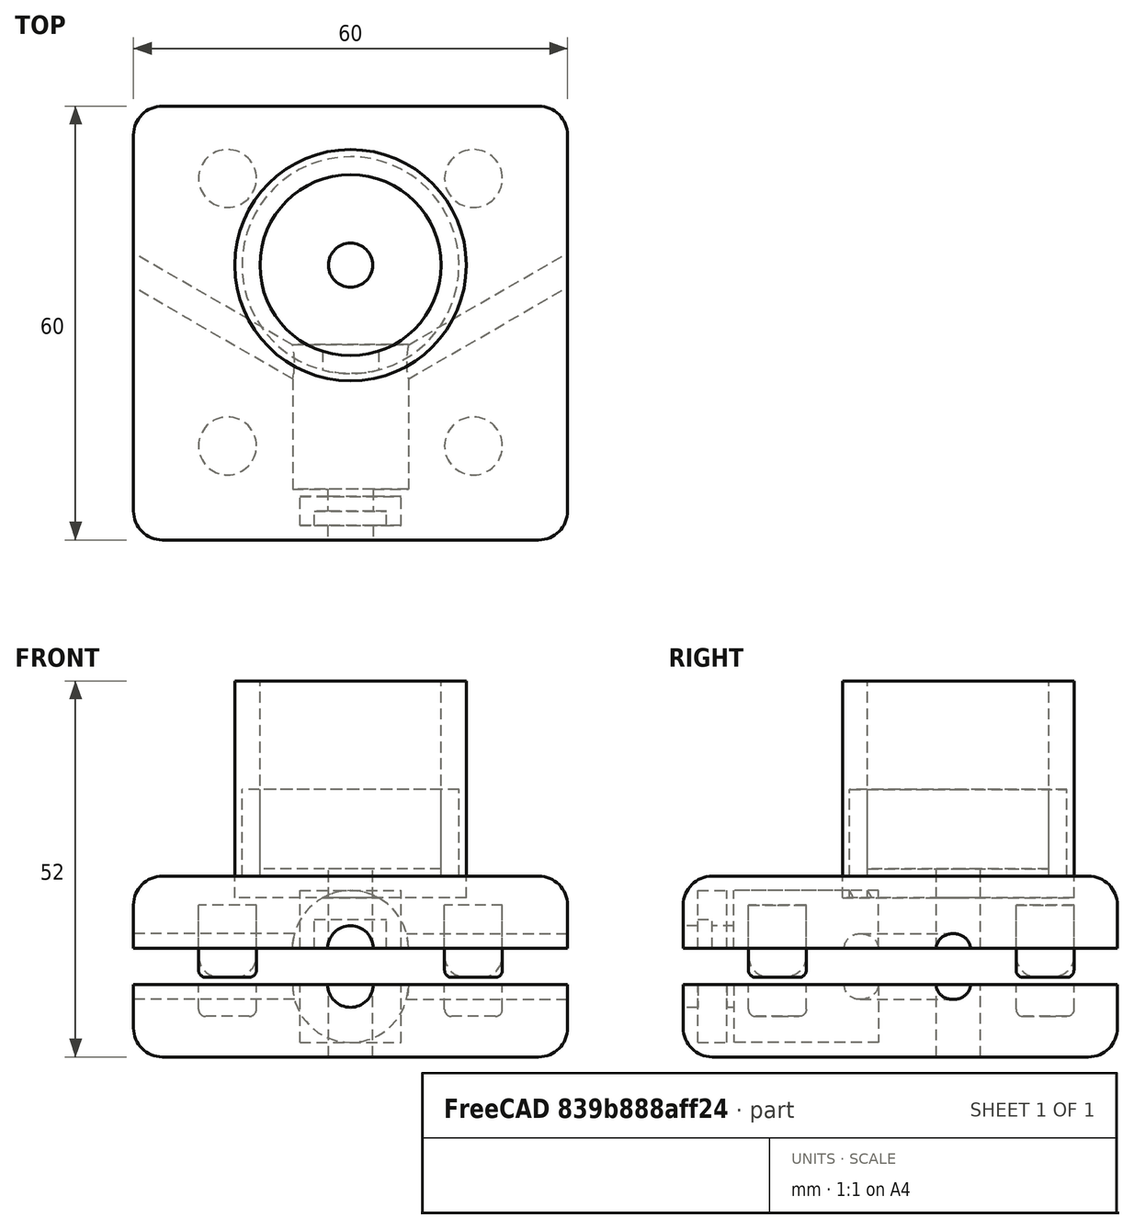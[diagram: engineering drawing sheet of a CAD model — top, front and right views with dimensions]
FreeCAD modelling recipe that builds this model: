
FCSTD DOCUMENT  (FreeCAD 0.18R4 (GitTag))
Label: V-Dipole_VHF_v07
License: All rights reserved
LicenseURL: http://en.wikipedia.org/wiki/All_rights_reserved
objects: Part::Cylinder×32, Part::Fillet×15, Part::MultiFuse×11, Part::Cut×10, Part::Box×6
note: 74 computed .brp shape members not serialized (recipe doc carries the construction recipe); baked Part::Feature solids carry a one-line shape summary decoded from their .brp

FEATURE [Part::Box] Box  label="Cubo"
  AttacherType = Attacher::AttachEngine3D
  Height = 10
  Length = 60
  Width = 60
FEATURE [Part::Fillet] Fillet  label="FilletA"
  Base = -> Box
  Edges = 8 edges r=4: [Edge1,Edge2,Edge3,Edge5,Edge6,Edge7,Edge10,Edge12]
FEATURE [Part::Box] Box001  label="Cubo001"
  AttacherType = Attacher::AttachEngine3D
  Height = 10
  Length = 60
  Width = 60
FEATURE [Part::Fillet] Fillet001  label="FilletB"
  Base = -> Box001
  Edges = 8 edges r=4: [Edge1,Edge2,Edge3,Edge5,Edge6,Edge7,Edge10,Edge12]
  Placement = pos=(0,60,-5) rot=(1,0,0;3.14159rad)
FEATURE [Part::Cylinder] Cylinder017  label="RamoA1"
  Angle = 360
  AttacherType = Attacher::AttachEngine3D
  Height = 100
  Placement = pos=(30,20,0) rot=(-0.774597,-0.447214,0.447214;1.82348rad)
  Radius = 2.05
FEATURE [Part::Cylinder] Cylinder018  label="RamoA2"
  Angle = 360
  AttacherType = Attacher::AttachEngine3D
  Height = 100
  Placement = pos=(30,20,0) rot=(-0.774597,0.447214,-0.447214;1.82348rad)
  Radius = 2.05
FEATURE [Part::Cylinder] Cylinder019  label="RamoB1"
  Angle = 360
  AttacherType = Attacher::AttachEngine3D
  Height = 100
  Placement = pos=(30,20,-5) rot=(-0.774597,-0.447214,0.447214;1.82348rad)
  Radius = 2.05
FEATURE [Part::Cylinder] Cylinder020  label="RamoB2"
  Angle = 360
  AttacherType = Attacher::AttachEngine3D
  Height = 100
  Placement = pos=(30,20,-5) rot=(-0.774597,0.447214,-0.447214;1.82348rad)
  Radius = 2.05
FEATURE [Part::Cylinder] Cylinder003  label="ForoBM3"
  Angle = 360
  AttacherType = Attacher::AttachEngine3D
  Height = 60
  Placement = pos=(30,38,-30) rot=(0,0,1;0rad)
  Radius = 3.05
FEATURE [Part::Cylinder] Cylinder014  label="CilindroInterno"
  Angle = 360
  AttacherType = Attacher::AttachEngine3D
  Height = 17
  Placement = pos=(30,38,6) rot=(0,0,1;0rad)
  Radius = 12.52
FEATURE [Part::Cylinder] Cylinder015  label="CilindroEsterno"
  Angle = 360
  AttacherType = Attacher::AttachEngine3D
  Height = 15
  Placement = pos=(30,38,7) rot=(0,0,1;0rad)
  Radius = 15
FEATURE [Part::Cut] Cut019  label="Supporto"
  Base = -> Cylinder015
  Tool = -> Cylinder014
FEATURE [Part::Cylinder] Cylinder  label="CilindroA"
  Angle = 360
  AttacherType = Attacher::AttachEngine3D
  Height = 26
  Placement = pos=(30,24,0) rot=(1,0,0;1.5708rad)
  Radius = 3.15
FEATURE [Part::Cylinder] Cylinder016  label="CilindroB"
  Angle = 360
  AttacherType = Attacher::AttachEngine3D
  Height = 26
  Placement = pos=(30,24,-5) rot=(1,0,0;1.5708rad)
  Radius = 3.15
FEATURE [Part::Box] Box005  label="CuboA"
  AttacherType = Attacher::AttachEngine3D
  Height = 8
  Length = 10
  Placement = pos=(25,2,-4) rot=(0,0,1;0rad)
  Width = 2
FEATURE [Part::Box] Box006  label="CuboB"
  AttacherType = Attacher::AttachEngine3D
  Height = 12
  Length = 14
  Placement = pos=(23,2,-13) rot=(0,0,1;0rad)
  Width = 4
FEATURE [Part::Cylinder] Cylinder021  label="CilindroA2"
  Angle = 360
  AttacherType = Attacher::AttachEngine3D
  Height = 20
  Placement = pos=(30,27,0) rot=(1,0,0;1.5708rad)
  Radius = 8
FEATURE [Part::MultiFuse] Fusion  label="FusionA"
  Shapes = -> [Cylinder017,Cylinder018,Cylinder,Box005,Cylinder021]
FEATURE [Part::Cylinder] Cylinder022  label="CilindroB2"
  Angle = 360
  AttacherType = Attacher::AttachEngine3D
  Height = 20
  Placement = pos=(30,27,-5) rot=(1,0,0;1.5708rad)
  Radius = 8
FEATURE [Part::MultiFuse] Fusion001
  Shapes = -> [Cylinder019,Cylinder020,Cylinder016,Box006,Cylinder022]
FEATURE [Part::Cut] Cut  label="FusionB"
  Base = -> Fillet001
  Tool = -> Fusion001
FEATURE [Part::Cylinder] Cylinder023  label="ForoAM3"
  Angle = 360
  AttacherType = Attacher::AttachEngine3D
  Height = 60
  Placement = pos=(30,38,-30) rot=(0,0,1;0rad)
  Radius = 3.05
FEATURE [Part::Cut] Cut020  label="ConchigliaB"
  Base = -> Cut
  Tool = -> Cylinder003
FEATURE [Part::Cut] Cut021
  Base = -> Fillet
  Tool = -> Fusion
FEATURE [Part::Cut] Cut022
  Base = -> Cut021
  Tool = -> Cylinder023
FEATURE [Part::MultiFuse] Fusion002  label="ConchigliaA"
  Shapes = -> [Cut019,Cut022]
FEATURE [Part::Cylinder] Cylinder024  label="CilindroA10"
  Angle = 360
  AttacherType = Attacher::AttachEngine3D
  Height = 10
  Placement = pos=(13,13,-4) rot=(0,0,1;0rad)
  Radius = 4
FEATURE [Part::Cylinder] Cylinder025  label="CilindroA11"
  Angle = 360
  AttacherType = Attacher::AttachEngine3D
  Height = 10
  Placement = pos=(47,13,-4) rot=(0,0,1;0rad)
  Radius = 4
FEATURE [Part::Fillet] Fillet002
  Base = -> Cylinder024
  Edges = 1 edges r=3: [Edge3]
FEATURE [Part::Fillet] Fillet003
  Base = -> Cylinder025
  Edges = 1 edges r=3: [Edge3]
FEATURE [Part::Cylinder] Cylinder026  label="CilindroA012"
  Angle = 360
  AttacherType = Attacher::AttachEngine3D
  Height = 10
  Placement = pos=(13,13,-4) rot=(0,0,1;0rad)
  Radius = 4
FEATURE [Part::Cylinder] Cylinder027  label="CilindroA013"
  Angle = 360
  AttacherType = Attacher::AttachEngine3D
  Height = 10
  Placement = pos=(47,13,-4) rot=(0,0,1;0rad)
  Radius = 4
FEATURE [Part::Fillet] Fillet004
  Base = -> Cylinder027
  Edges = 1 edges r=3: [Edge3]
  Placement = pos=(0,37,0) rot=(0,0,1;0rad)
FEATURE [Part::Fillet] Fillet005
  Base = -> Cylinder026
  Edges = 1 edges r=3: [Edge3]
  Placement = pos=(0,37,0) rot=(0,0,1;0rad)
FEATURE [Part::Cylinder] Cylinder028  label="CilindroA014"
  Angle = 360
  AttacherType = Attacher::AttachEngine3D
  Height = 10
  Placement = pos=(13,13,-4) rot=(0,0,1;0rad)
  Radius = 4
FEATURE [Part::Cylinder] Cylinder029  label="CilindroA015"
  Angle = 360
  AttacherType = Attacher::AttachEngine3D
  Height = 10
  Placement = pos=(13,13,-4) rot=(0,0,1;0rad)
  Radius = 4
FEATURE [Part::Cylinder] Cylinder030  label="CilindroA016"
  Angle = 360
  AttacherType = Attacher::AttachEngine3D
  Height = 10
  Placement = pos=(47,13,-4) rot=(0,0,1;0rad)
  Radius = 4
FEATURE [Part::Cylinder] Cylinder031  label="CilindroA017"
  Angle = 360
  AttacherType = Attacher::AttachEngine3D
  Height = 10
  Placement = pos=(47,13,-4) rot=(0,0,1;0rad)
  Radius = 4
FEATURE [Part::Fillet] Fillet006
  Base = -> Cylinder029
  Edges = 1 edges r=1: [Edge3]
  Placement = pos=(0,37,0) rot=(0,0,1;0rad)
FEATURE [Part::Fillet] Fillet007
  Base = -> Cylinder030
  Edges = 1 edges r=1: [Edge3]
FEATURE [Part::Fillet] Fillet008
  Base = -> Cylinder028
  Edges = 1 edges r=1: [Edge3]
FEATURE [Part::Fillet] Fillet009
  Base = -> Cylinder031
  Edges = 1 edges r=1: [Edge3]
  Placement = pos=(0,37,0) rot=(0,0,1;0rad)
FEATURE [Part::MultiFuse] Fusion004
  Shapes = -> [Fillet002,Fillet003,Fillet004,Fillet005]
FEATURE [Part::MultiFuse] Fusion005  label="ConchigliaAAA_err"
  Shapes = -> [Fusion002,Fusion004]
FEATURE [Part::MultiFuse] Fusion006
  Placement = pos=(0,0,-5.4) rot=(0,0,1;0rad)
  Shapes = -> [Fillet006,Fillet007,Fillet008,Fillet009]
FEATURE [Part::Cut] Cut023  label="ConchigliaBBB"
  Base = -> Cut020
  Tool = -> Fusion006
FEATURE [Part::MultiFuse] Fusion003
  Shapes = -> [Fillet006,Fillet007,Fillet008,Fillet009]
FEATURE [Part::MultiFuse] Fusion007
  Shapes = -> [Fillet006,Fillet007,Fillet008,Fillet009]
FEATURE [Part::Cylinder] Cylinder032  label="CilindroA018"
  Angle = 360
  AttacherType = Attacher::AttachEngine3D
  Height = 26
  Placement = pos=(30,24,0) rot=(1,0,0;1.5708rad)
  Radius = 3.15
FEATURE [Part::Cylinder] Cylinder033  label="CilindroA019"
  Angle = 360
  AttacherType = Attacher::AttachEngine3D
  Height = 20
  Placement = pos=(30,27,0) rot=(1,0,0;1.5708rad)
  Radius = 8
FEATURE [Part::Box] Box007  label="Cubo002"
  AttacherType = Attacher::AttachEngine3D
  Height = 10
  Length = 60
  Width = 60
FEATURE [Part::Fillet] Fillet010  label="FilletA001"
  Base = -> Box007
  Edges = 8 edges r=4: [Edge1,Edge2,Edge3,Edge5,Edge6,Edge7,Edge10,Edge12]
FEATURE [Part::Cylinder] Cylinder034  label="RamoA003"
  Angle = 360
  AttacherType = Attacher::AttachEngine3D
  Height = 100
  Placement = pos=(30,20,0) rot=(-0.774597,-0.447214,0.447214;1.82348rad)
  Radius = 2.05
FEATURE [Part::Box] Box008  label="CuboA001"
  AttacherType = Attacher::AttachEngine3D
  Height = 12
  Length = 14
  Placement = pos=(23,2,-4) rot=(0,0,1;0rad)
  Width = 4
FEATURE [Part::Cylinder] Cylinder035  label="RamoA004"
  Angle = 360
  AttacherType = Attacher::AttachEngine3D
  Height = 100
  Placement = pos=(30,20,0) rot=(-0.774597,0.447214,-0.447214;1.82348rad)
  Radius = 2.05
FEATURE [Part::Cylinder] Cylinder036  label="ForoAM004"
  Angle = 360
  AttacherType = Attacher::AttachEngine3D
  Height = 60
  Placement = pos=(30,38,-30) rot=(0,0,1;0rad)
  Radius = 3.05
FEATURE [Part::MultiFuse] Fusion008  label="FusionA001"
  Shapes = -> [Cylinder034,Cylinder035,Cylinder032,Box008,Cylinder033]
FEATURE [Part::Cut] Cut025
  Base = -> Fillet010
  Tool = -> Fusion008
FEATURE [Part::Cut] Cut024
  Base = -> Cut025
  Tool = -> Cylinder036
FEATURE [Part::Cylinder] Cylinder037  label="CilindroEsterno001"
  Angle = 360
  AttacherType = Attacher::AttachEngine3D
  Height = 30
  Placement = pos=(30,38,7) rot=(0,0,1;0rad)
  Radius = 16
FEATURE [Part::Cylinder] Cylinder038  label="CilindroInterno001"
  Angle = 360
  AttacherType = Attacher::AttachEngine3D
  Height = 27
  Placement = pos=(30,38,11) rot=(0,0,1;0rad)
  Radius = 12.52
FEATURE [Part::Cut] Cut026  label="Supporto001"
  Base = -> Cylinder037
  Tool = -> Cylinder038
FEATURE [Part::Cylinder] Cylinder039  label="CilindroA020"
  Angle = 360
  AttacherType = Attacher::AttachEngine3D
  Height = 10
  Placement = pos=(47,13,-4) rot=(0,0,1;0rad)
  Radius = 4
FEATURE [Part::Fillet] Fillet012
  Base = -> Cylinder039
  Edges = 1 edges r=3: [Edge3]
  Placement = pos=(0,37,0) rot=(0,0,1;0rad)
FEATURE [Part::Cylinder] Cylinder040  label="CilindroA021"
  Angle = 360
  AttacherType = Attacher::AttachEngine3D
  Height = 10
  Placement = pos=(13,13,-4) rot=(0,0,1;0rad)
  Radius = 4
FEATURE [Part::Fillet] Fillet013
  Base = -> Cylinder040
  Edges = 1 edges r=3: [Edge3]
FEATURE [Part::Cylinder] Cylinder041  label="CilindroA022"
  Angle = 360
  AttacherType = Attacher::AttachEngine3D
  Height = 10
  Placement = pos=(47,13,-4) rot=(0,0,1;0rad)
  Radius = 4
FEATURE [Part::Fillet] Fillet011
  Base = -> Cylinder041
  Edges = 1 edges r=3: [Edge3]
FEATURE [Part::Cylinder] Cylinder042  label="CilindroA023"
  Angle = 360
  AttacherType = Attacher::AttachEngine3D
  Height = 10
  Placement = pos=(13,13,-4) rot=(0,0,1;0rad)
  Radius = 4
FEATURE [Part::Fillet] Fillet014
  Base = -> Cylinder042
  Edges = 1 edges r=3: [Edge3]
  Placement = pos=(0,37,0) rot=(0,0,1;0rad)
FEATURE [Part::MultiFuse] Fusion009
  Shapes = -> [Fillet013,Fillet011,Fillet012,Fillet014]
FEATURE [Part::MultiFuse] Fusion010  label="ConchigliaAAA"
  Shapes = -> [Cut024,Fusion009]
FEATURE [Part::Cylinder] Cylinder043  label="ForoBM004"
  Angle = 360
  AttacherType = Attacher::AttachEngine3D
  Height = 30
  Placement = pos=(30,38,-6) rot=(0,0,1;0rad)
  Radius = 3.05
FEATURE [Part::Cut] Cut027  label="SupportoPalo"
  Base = -> Cut026
  Tool = -> Cylinder043
